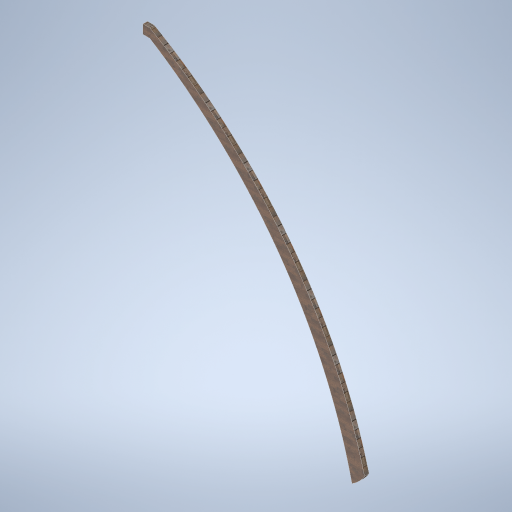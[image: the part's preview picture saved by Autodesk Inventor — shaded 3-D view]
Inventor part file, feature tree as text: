
AUTODESK INVENTOR PART (.ipt)
format: ipt  version: 2024.2 (Build 282272000, 272)  size: 279,552 bytes
history: native  units: mm
features: extrude x1, sketch x1
ambient origin geometry x8: Origin, YZ Plane, XZ Plane, XY Plane, X Axis, Y Axis, Z Axis, Center Point
bodies: Solid1 (feature_tree)
feature tree (2):
  extrude  "Extrusion1"  Depth=100.0mm
  sketch  "Sketch1"  dims[d0=10000.0mm d1=10000.0mm d2=150.0mm d3=100.0mm d4=0.0mm]
